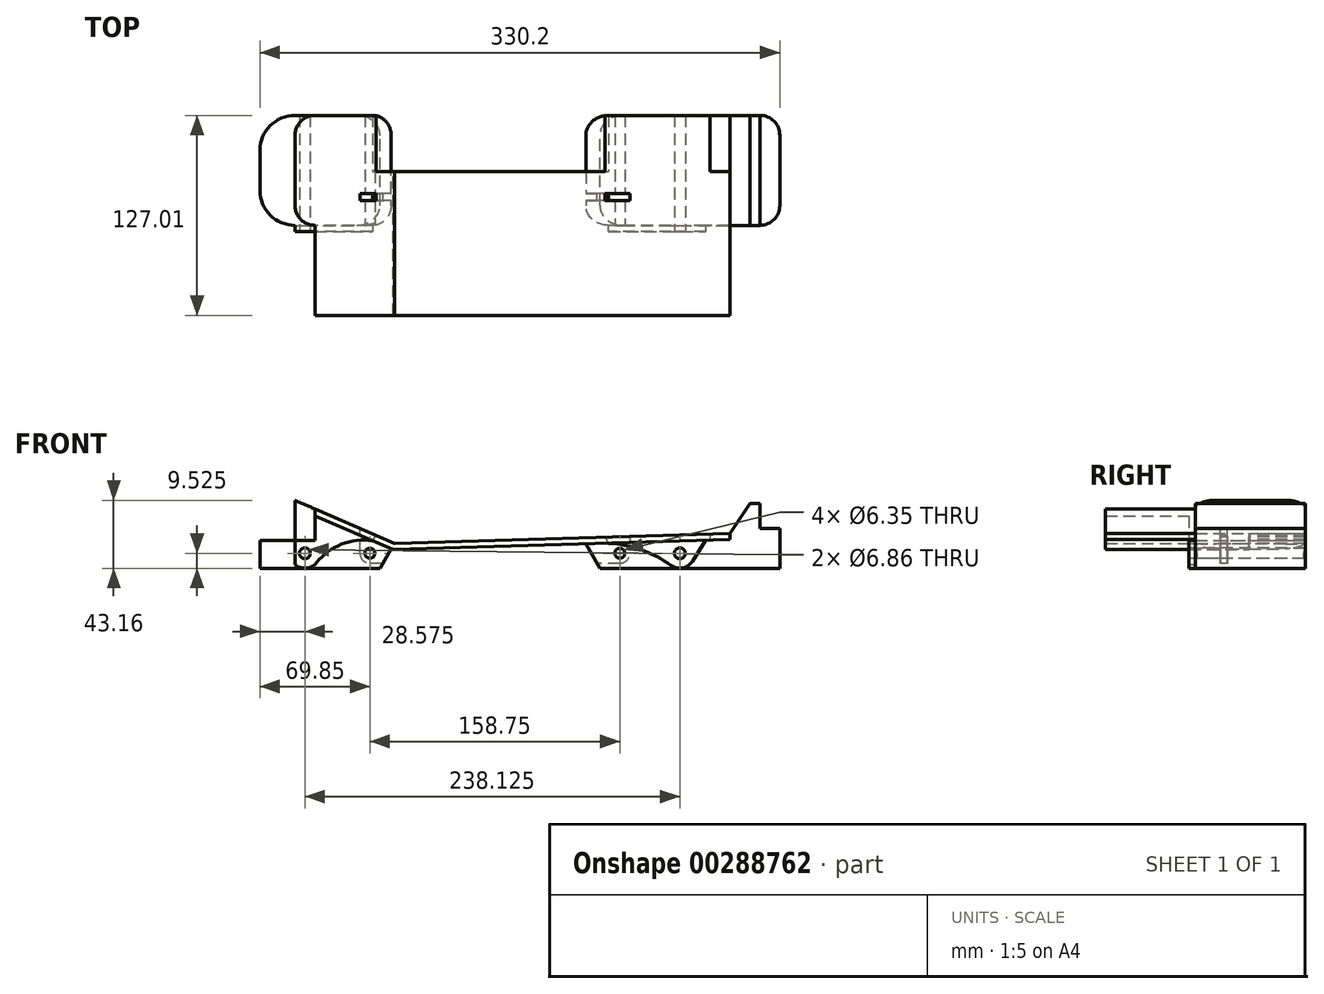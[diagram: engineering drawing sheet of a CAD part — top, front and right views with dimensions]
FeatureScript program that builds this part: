
annotation { "Feature Type Name" : "Feature", "Feature Type Description" : "" }
export const myFeature = defineFeature(function(context is Context, id is Id, definition is map)
    precondition{}
    {
        {
            var Q0;
            Q0=qCreatedBy(makeId("Front.planeOp"),FACE);
            var sketch = newSketch(context, id + "F0", { "sketchPlane" : qUnion([Q0])});
            skLineSegment(sketch, "E0", {"start": v(0, 0) * mm, "end": v(76.2, 0) * mm});
            skLineSegment(sketch, "E1", {"start": v(22.22, 43.16) * mm, "end": v(22.23, 17.76) * mm});
            skLineSegment(sketch, "E2", {"start": v(22.23, 17.76) * mm, "end": v(0, 17.76) * mm});
            skLineSegment(sketch, "E3", {"start": v(0, 17.76) * mm, "end": v(0, 0) * mm});
            skLineSegment(sketch, "E4", {"start": v(215.9, 0) * mm, "end": v(330.2, 0) * mm});
            skLineSegment(sketch, "E5", {"start": v(330.2, 0) * mm, "end": v(330.2, 25.4) * mm});
            skLineSegment(sketch, "E6", {"start": v(330.2, 25.4) * mm, "end": v(317.5, 25.4) * mm});
            skLineSegment(sketch, "E7", {"start": v(317.5, 25.4) * mm, "end": v(317.5, 41.28) * mm});
            skLineSegment(sketch, "E8", {"start": v(317.5, 41.28) * mm, "end": v(311.15, 41.28) * mm});
            skLineSegment(sketch, "E9", {"start": v(311.15, 41.27) * mm, "end": v(298.45, 22.22) * mm});
            skLineSegment(sketch, "E10", {"start": v(215.9, 0) * mm, "end": v(204.68, 19.43) * mm});
            skLineSegment(sketch, "E11", {"start": v(85.37, 15.88) * mm, "end": v(76.2, 0) * mm});
            skLineSegment(sketch, "E12", {"start": v(85.37, 15.88) * mm, "end": v(298.45, 22.23) * mm, "construction": true});
            skLineSegment(sketch, "E13", {"start": v(204.68, 19.43) * mm, "end": v(298.45, 22.23) * mm});
            skLineSegment(sketch, "E14", {"start": v(85.37, 15.88) * mm, "end": v(22.23, 43.16) * mm});
            skSolve(sketch);
        }
        {
            var Q0;
            Q0 = qSketchRegion(id + "F0", true);
            extrude(context, id + "F1", {"entities" : qUnion([Q0]), "endBound" : BoundingType.SYMMETRIC, "depth" : 69.85 * mm});
        }
        {
            var Q0;
            Q0=makeQuery(id+"F1.opExtrude","CAP_EDGE",EDGE,{"disambiguationData":[OSD([sQuery(id+"F0.wireOp",EDGE,"E5")])],"isStart":false});
            var Q1;
            Q1=makeQuery(id+"F1.opExtrude","CAP_EDGE",EDGE,{"disambiguationData":[OSD([sQuery(id+"F0.wireOp",EDGE,"E5")])],"isStart":true});
            fillet(context, id + "F2", {"entities" : qUnion([Q0, Q1]), "radius" : 12.7 * mm, "tangentPropagation" : true, "allowEdgeOverflow" : false});
        }
        {
            var Q0;
            Q0=makeQuery(id+"F1.opExtrude","CAP_EDGE",EDGE,{"disambiguationData":[OSD([sQuery(id+"F0.wireOp",EDGE,"E3")])],"isStart":true});
            var Q1;
            Q1=makeQuery(id+"F1.opExtrude","CAP_EDGE",EDGE,{"disambiguationData":[OSD([sQuery(id+"F0.wireOp",EDGE,"E3")])],"isStart":false});
            fillet(context, id + "F3", {"entities" : qUnion([Q0, Q1]), "radius" : 22.22 * mm, "tangentPropagation" : true, "allowEdgeOverflow" : false});
        }
        {
            var Q0;
            Q0=qCreatedBy(makeId("Front.planeOp"),FACE);
            var sketch = newSketch(context, id + "F4", { "sketchPlane" : qUnion([Q0])});
            skCircle(sketch, "E15", {"center": v(28.58, 9.53) * mm, "radius": 3.43 * mm});
            skLineSegment(sketch, "E16", {"start": v(1.33, 9.53) * mm, "end": v(325.3, 9.53) * mm, "construction": true});
            skCircle(sketch, "E17", {"center": v(266.7, 9.53) * mm, "radius": 3.43 * mm});
            skCircle(sketch, "E18", {"center": v(228.6, 9.53) * mm, "radius": 3.18 * mm});
            skCircle(sketch, "E19", {"center": v(69.85, 9.53) * mm, "radius": 3.18 * mm});
            skLineSegment(sketch, "E20.0", {"start": v(204.68, 19.43) * mm, "end": v(298.45, 22.23) * mm});
            skLineSegment(sketch, "E21", {"start": v(298.45, 22.23) * mm, "end": v(298.57, 18.16) * mm});
            skLineSegment(sketch, "E22", {"start": v(298.57, 18.16) * mm, "end": v(285.88, 17.78) * mm});
            skLineSegment(sketch, "E23", {"start": v(285.88, 17.78) * mm, "end": v(285.76, 21.85) * mm});
            skSolve(sketch);
        }
        {
            var Q0;
            Q0 = qSketchRegion(id + "F4", true);
            extrude(context, id + "F5", {"entities" : qUnion([Q0]), "operationType" : NewBodyOperationType.REMOVE, "endBound" : BoundingType.SYMMETRIC, "oppositeDirection" : true, "depth" : 76.2 * mm});
        }
        {
            var Q0;
            Q0=qCreatedBy(makeId("Front.planeOp"),FACE);
            cPlane(context, id + "F6", {"entities" : qUnion([Q0]), "cplaneType" : CPlaneType.OFFSET, "offset" : 19.05 * mm, "width" : 152.4 * mm, "height" : 152.4 * mm});
        }
        {
            var Q0;
            Q0=qCreatedBy(id+"F6.planeOp",FACE);
            var sketch = newSketch(context, id + "F7", { "sketchPlane" : qUnion([Q0])});
            skCircle(sketch, "E24.0", {"center": v(228.6, 9.53) * mm, "radius": 3.18 * mm});
            skCircle(sketch, "E24.1", {"center": v(69.85, 9.53) * mm, "radius": 3.18 * mm});
            skLineSegment(sketch, "E25", {"start": v(258.75, 0) * mm, "end": v(45.97, 0) * mm, "construction": true});
            skArc(sketch, "E26", {"start": v(228.6, 3.17) * mm, "mid": v(234.95, 9.53) * mm, "end": v(228.6, 15.88) * mm});
            skArc(sketch, "E27", {"start": v(69.85, 15.88) * mm, "mid": v(63.5, 9.53) * mm, "end": v(69.85, 3.17) * mm});
            skPoint(sketch, "E28.0", {"position": v(85.37, 15.88) * mm});
            skLineSegment(sketch, "E29", {"start": v(228.6, 15.88) * mm, "end": v(69.85, 15.88) * mm});
            skLineSegment(sketch, "E30", {"start": v(228.6, 3.18) * mm, "end": v(69.85, 3.17) * mm});
            skLineSegment(sketch, "E31", {"start": v(63.5, 0) * mm, "end": v(234.95, 0) * mm});
            skPoint(sketch, "E31.endSnap0", {"position": v(234.95, 9.53) * mm});
            skLineSegment(sketch, "E32", {"start": v(63.5, 9.52) * mm, "end": v(63.5, 55.73) * mm});
            skLineSegment(sketch, "E33", {"start": v(63.5, 55.73) * mm, "end": v(234.95, 55.73) * mm});
            skLineSegment(sketch, "E34", {"start": v(234.95, 55.73) * mm, "end": v(234.95, 9.52) * mm});
            skSolve(sketch);
        }
        {
            var Q0;
            Q0 = qSketchRegion(id + "F7", true);
            extrude(context, id + "F8", {"entities" : qUnion([Q0]), "operationType" : NewBodyOperationType.REMOVE, "oppositeDirection" : true, "depth" : 4.32 * mm});
        }
        {
            var Q0;
            Q0=makeQuery(id+"F1.opExtrude","CAP_EDGE",EDGE,{"disambiguationData":[OSD([sQuery(id+"F0.wireOp",EDGE,"E11")])],"isStart":false});
            var Q1;
            Q1=makeQuery(id+"F1.opExtrude","CAP_EDGE",EDGE,{"disambiguationData":[OSD([sQuery(id+"F0.wireOp",EDGE,"E11")])],"isStart":true});
            var Q2;
            Q2=makeQuery(id+"F1.opExtrude","CAP_EDGE",EDGE,{"disambiguationData":[OSD([sQuery(id+"F0.wireOp",EDGE,"E10")])],"isStart":false});
            var Q3;
            Q3=makeQuery(id+"F1.opExtrude","CAP_EDGE",EDGE,{"disambiguationData":[OSD([sQuery(id+"F0.wireOp",EDGE,"E10")])],"isStart":true});
            fillet(context, id + "F9", {"entities" : qUnion([Q0, Q1, Q2, Q3]), "radius" : 12.7 * mm, "tangentPropagation" : true, "allowEdgeOverflow" : false});
        }
        {
            var Q0;
            Q0=makeQuery(id+"F1.opExtrude","CAP_EDGE",EDGE,{"disambiguationData":[OSD([sQuery(id+"F0.wireOp",EDGE,"E1")])],"isStart":false});
            var Q1;
            Q1=makeQuery(id+"F1.opExtrude","CAP_EDGE",EDGE,{"disambiguationData":[OSD([sQuery(id+"F0.wireOp",EDGE,"E1")])],"isStart":true});
            fillet(context, id + "F10", {"entities" : qUnion([Q0, Q1]), "radius" : 12.7 * mm, "tangentPropagation" : true, "allowEdgeOverflow" : false});
        }
        {
            var Q0;
            Q0=makeQuery(id+"F1.opExtrude","CAP_FACE",FACE,{"disambiguationData":[OSD([sQuery(id+"F0.wireOp",EDGE,"E0"),sQuery(id+"F0.wireOp",EDGE,"E1"),sQuery(id+"F0.wireOp",EDGE,"E2"),sQuery(id+"F0.wireOp",EDGE,"E3"),sQuery(id+"F0.wireOp",EDGE,"E11"),sQuery(id+"F0.wireOp",EDGE,"E14")])],"isStart":false});
            var sketch = newSketch(context, id + "F11", { "sketchPlane" : qUnion([Q0])});
            skArc(sketch, "E35", {"start": v(22.22, 2.43) * mm, "mid": v(29.37, 0.03) * mm, "end": v(36.01, 3.58) * mm});
            skLineSegment(sketch, "E36", {"start": v(22.22, 2.43) * mm, "end": v(22.22, 17.76) * mm});
            skLineSegment(sketch, "E37", {"start": v(22.23, 17.76) * mm, "end": v(34.92, 17.76) * mm});
            skLineSegment(sketch, "E38", {"start": v(34.92, 17.76) * mm, "end": v(34.92, 37.67) * mm});
            skLineSegment(sketch, "E39", {"start": v(34.92, 37.67) * mm, "end": v(73.63, 20.95) * mm});
            skCircle(sketch, "E40.0", {"center": v(266.7, 9.53) * mm, "radius": 3.43 * mm});
            skArc(sketch, "E41", {"start": v(261.16, 1.78) * mm, "mid": v(268.53, 0.18) * mm, "end": v(274.75, 4.44) * mm});
            skLineSegment(sketch, "E42.0", {"start": v(68.76, 12.5) * mm, "end": v(73.63, 20.95) * mm});
            skLineSegment(sketch, "E43.0", {"start": v(219.1, 19.86) * mm, "end": v(285.75, 21.85) * mm});
            skLineSegment(sketch, "E44", {"start": v(285.75, 21.85) * mm, "end": v(274.75, 4.44) * mm});
            skCircle(sketch, "E45.0", {"center": v(28.58, 9.53) * mm, "radius": 3.43 * mm});
            skArc(sketch, "E46", {"start": v(71.6, 17.43) * mm, "mid": v(51.94, 15.28) * mm, "end": v(36.01, 3.58) * mm});
            skLineSegment(sketch, "E47", {"start": v(73.63, 20.95) * mm, "end": v(71.6, 17.43) * mm});
            skLineSegment(sketch, "E48", {"start": v(219.1, 19.86) * mm, "end": v(221.4, 15.86) * mm});
            skArc(sketch, "E49", {"start": v(261.16, 1.78) * mm, "mid": v(242.28, 11.63) * mm, "end": v(221.4, 15.86) * mm});
            skSolve(sketch);
        }
        {
            var Q0;
            Q0 = qSketchRegion(id + "F11", true);
            extrude(context, id + "F12", {"entities" : qUnion([Q0]), "depth" : 4.06 * mm});
        }
        {
            var Q0;
            Q0=makeQuery(id+"F12.opExtrude","CAP_FACE",FACE,{"disambiguationData":[OSD([sQuery(id+"F11.wireOp",EDGE,"E35"),sQuery(id+"F11.wireOp",EDGE,"E36"),sQuery(id+"F11.wireOp",EDGE,"E37"),sQuery(id+"F11.wireOp",EDGE,"E38"),sQuery(id+"F11.wireOp",EDGE,"E39"),sQuery(id+"F11.wireOp",EDGE,"E45.0"),sQuery(id+"F11.wireOp",EDGE,"E46"),sQuery(id+"F11.wireOp",EDGE,"E47")])],"isStart":false});
            var sketch = newSketch(context, id + "F13", { "sketchPlane" : qUnion([Q0])});
            skLineSegment(sketch, "E50", {"start": v(34.92, 37.67) * mm, "end": v(85.37, 15.87) * mm});
            skPoint(sketch, "E51.0", {"position": v(285.75, 21.85) * mm});
            skLineSegment(sketch, "E51.1", {"start": v(85.37, 15.87) * mm, "end": v(298.45, 22.23) * mm});
            skPoint(sketch, "E52.orphan", {"position": v(219.1, 19.86) * mm});
            skLineSegment(sketch, "E53.0", {"start": v(84.58, 11.79) * mm, "end": v(298.57, 18.16) * mm});
            skLineSegment(sketch, "E53.1", {"start": v(33.31, 33.94) * mm, "end": v(84.58, 11.79) * mm});
            skLineSegment(sketch, "E54", {"start": v(34.92, 37.67) * mm, "end": v(34.92, 33.24) * mm});
            skPoint(sketch, "E55.0", {"position": v(298.45, 22.23) * mm});
            skLineSegment(sketch, "E56", {"start": v(298.45, 22.23) * mm, "end": v(298.57, 18.16) * mm});
            skSolve(sketch);
        }
        {
            var Q0;
            Q0 = qSketchRegion(id + "F13", true);
            extrude(context, id + "F14", {"entities" : qUnion([Q0]), "operationType" : NewBodyOperationType.ADD, "depth" : 53.1 * mm});
        }
        {
            var Q0;
            {var subQ0=sQuery(id+"F13.wireOp",EDGE,"E50");var subQ2=sQuery(id+"F13.wireOp",EDGE,"E51.1");var subQ5=sQuery(id+"F11.wireOp",EDGE,"E39");var subQ8=sQuery(id+"F13.wireOp",EDGE,"E53.1");var subQ9=sQuery(id+"F13.wireOp",EDGE,"E53.0");Q0=makeQuery(id+"F14.boolean.opBoolean","SPLIT",FACE,{"disambiguationData":[TD([makeQuery(id+"F12.opExtrude","SWEPT_FACE",FACE,{"disambiguationData":[OSD([subQ5])]})])],"derivedFrom":makeQuery(id+"F14.opExtrude","CAP_FACE",FACE,{"disambiguationData":[OSD([subQ0,subQ2,subQ9,subQ8,sQuery(id+"F13.wireOp",EDGE,"E54"),sQuery(id+"F13.wireOp",EDGE,"E56")])],"isStart":true})});}
            var sketch = newSketch(context, id + "F15", { "sketchPlane" : qUnion([Q0])});
            skLineSegment(sketch, "E57.0", {"start": v(-73.63, 20.95) * mm, "end": v(-85.37, 15.87) * mm});
            skLineSegment(sketch, "E57.1", {"start": v(-71.5, 17.44) * mm, "end": v(-84.58, 11.79) * mm});
            skLineSegment(sketch, "E58.0", {"start": v(-71.6, 17.43) * mm, "end": v(-73.63, 20.95) * mm});
            skLineSegment(sketch, "E59.0", {"start": v(-84.58, 11.79) * mm, "end": v(-221.4, 15.86) * mm});
            skLineSegment(sketch, "E59.1", {"start": v(-85.37, 15.87) * mm, "end": v(-219.1, 19.86) * mm});
            skLineSegment(sketch, "E59.2", {"start": v(-219.1, 19.86) * mm, "end": v(-221.4, 15.86) * mm});
            skSolve(sketch);
        }
        {
            var Q0;
            Q0=makeQuery(id+"F15.imprint","IMPRINT",FACE,{"disambiguationData":[TD([[makeQuery(id+"F15.imprint","IMPRINT",EDGE,{"derivedFrom":sQuery(id+"F15.wireOp",EDGE,"E57.0")}),1.0]])]});
            extrude(context, id + "F16", {"entities" : qUnion([Q0]), "operationType" : NewBodyOperationType.REMOVE, "depth" : 90.68 * mm});
        }
        {
            var Q0;
            {var subQ0=sQuery(id+"F13.wireOp",EDGE,"E50");var subQ2=sQuery(id+"F13.wireOp",EDGE,"E51.1");var subQ5=sQuery(id+"F11.wireOp",EDGE,"E39");var subQ8=sQuery(id+"F13.wireOp",EDGE,"E53.1");var subQ9=sQuery(id+"F13.wireOp",EDGE,"E53.0");Q0=makeQuery(id+"F14.boolean.opBoolean","SPLIT",FACE,{"disambiguationData":[TD([makeQuery(id+"F12.opExtrude","SWEPT_FACE",FACE,{"disambiguationData":[OSD([subQ5])]})])],"derivedFrom":makeQuery(id+"F14.opExtrude","CAP_FACE",FACE,{"disambiguationData":[OSD([subQ0,subQ2,subQ9,subQ8,sQuery(id+"F13.wireOp",EDGE,"E54"),sQuery(id+"F13.wireOp",EDGE,"E56")])],"isStart":true})});}
            var sketch = newSketch(context, id + "F17", { "sketchPlane" : qUnion([Q0])});
            skLineSegment(sketch, "E60.0", {"start": v(-84.58, 11.79) * mm, "end": v(-221.4, 15.86) * mm});
            skLineSegment(sketch, "E60.1", {"start": v(-85.37, 15.87) * mm, "end": v(-219.1, 19.86) * mm});
            skLineSegment(sketch, "E60.2", {"start": v(-73.63, 20.95) * mm, "end": v(-85.37, 15.87) * mm});
            skLineSegment(sketch, "E60.3", {"start": v(-71.5, 17.44) * mm, "end": v(-84.58, 11.79) * mm});
            skLineSegment(sketch, "E60.4", {"start": v(-71.6, 17.43) * mm, "end": v(-73.63, 20.95) * mm});
            skLineSegment(sketch, "E61.0", {"start": v(-219.1, 19.86) * mm, "end": v(-221.4, 15.86) * mm});
            skSolve(sketch);
        }
        {
            var Q0;
            Q0 = qSketchRegion(id + "F17", true);
            var Q1;
            {var subQ0=sQuery(id+"F17.wireOp",EDGE,"E60.2");Q1=makeQuery(id+"F17.imprint","IMPRINT",FACE,{"disambiguationData":[TD([[makeQuery(id+"F17.imprint","IMPRINT",EDGE,{"derivedFrom":subQ0}),1.0]])]});}
            var Q2;
            {var subQ0=sQuery(id+"F11.wireOp",EDGE,"E44");var subQ1=sQuery(id+"F13.wireOp",EDGE,"E51.1");var subQ3=sQuery(id+"F13.wireOp",EDGE,"E53.0");var subQ4=sQuery(id+"F13.wireOp",EDGE,"E56");Q2=makeQuery(id+"F14.boolean.opBoolean","SPLIT",FACE,{"disambiguationData":[TD([makeQuery(id+"F12.opExtrude","SWEPT_FACE",FACE,{"disambiguationData":[OSD([subQ0])]})])],"derivedFrom":makeQuery(id+"F14.opExtrude","CAP_FACE",FACE,{"disambiguationData":[OSD([sQuery(id+"F13.wireOp",EDGE,"E50"),subQ1,subQ3,sQuery(id+"F13.wireOp",EDGE,"E53.1"),sQuery(id+"F13.wireOp",EDGE,"E54"),subQ4])],"isStart":true})});}
            extrude(context, id + "F18", {"entities" : qUnion([Q0, Q1, Q2]), "operationType" : NewBodyOperationType.ADD, "depth" : 38.1 * mm});
        }
    });
